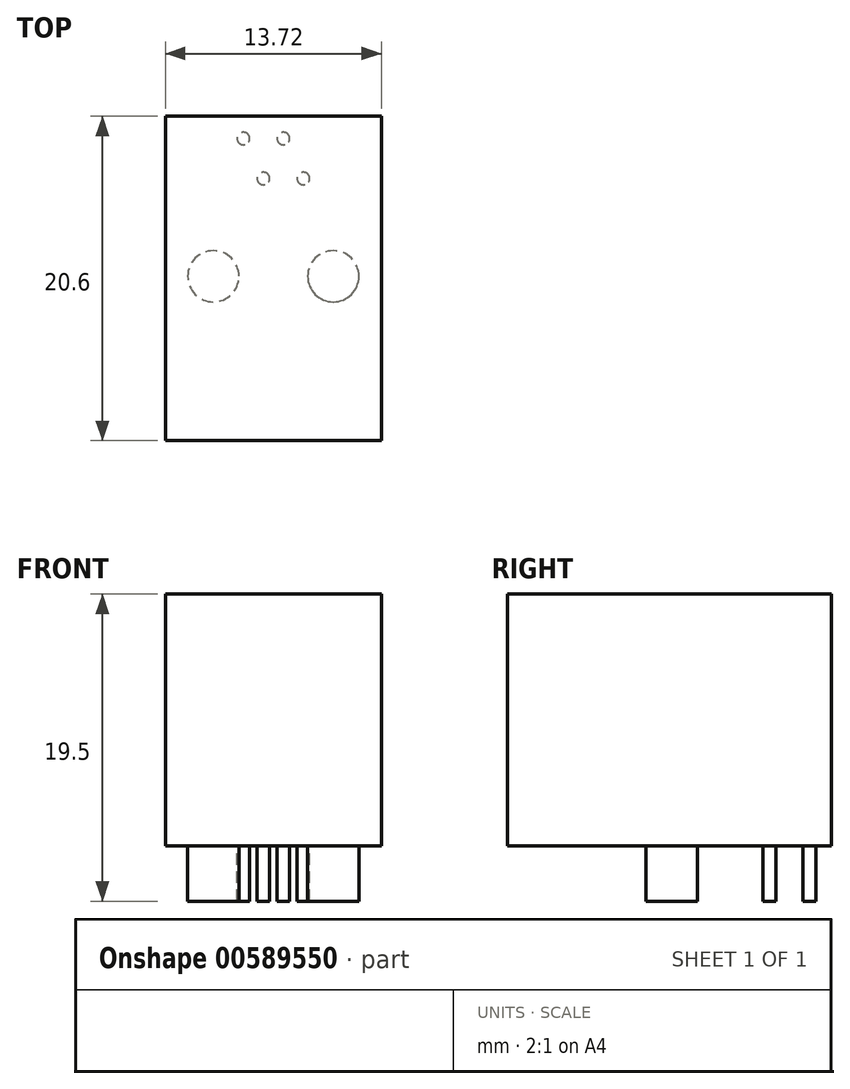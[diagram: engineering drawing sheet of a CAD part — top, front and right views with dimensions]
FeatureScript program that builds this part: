
annotation { "Feature Type Name" : "Feature", "Feature Type Description" : "" }
export const myFeature = defineFeature(function(context is Context, id is Id, definition is map)
    precondition{}
    {
        {
            var Q0;
            Q0=qCreatedBy(makeId("Top.planeOp"),FACE);
            var sketch = newSketch(context, id + "F0", { "sketchPlane" : qUnion([Q0])});
            skLineSegment(sketch, "E0.bottom", {"start": v(-6.86, 10.3) * mm, "end": v(6.86, 10.3) * mm});
            skLineSegment(sketch, "E0.top", {"start": v(-6.86, -10.3) * mm, "end": v(6.86, -10.3) * mm});
            skLineSegment(sketch, "E0.left", {"start": v(-6.86, 10.3) * mm, "end": v(-6.86, -10.3) * mm});
            skLineSegment(sketch, "E0.right", {"start": v(6.86, 10.3) * mm, "end": v(6.86, -10.3) * mm});
            skPoint(sketch, "E0.middle", {"position": v(0, 0) * mm});
            skSolve(sketch);
        }
        {
            var Q0;
            Q0 = qSketchRegion(id + "F0", true);
            extrude(context, id + "F1", {"entities" : qUnion([Q0]), "depth" : 16 * mm, "offsetDistance" : 25.4 * mm});
        }
        {
            var Q0;
            Q0=makeQuery(id+"F1.opExtrude","CAP_FACE",FACE,{"disambiguationData":[OSD([sQuery(id+"F0.wireOp",EDGE,"E0.bottom"),sQuery(id+"F0.wireOp",EDGE,"E0.top"),sQuery(id+"F0.wireOp",EDGE,"E0.left"),sQuery(id+"F0.wireOp",EDGE,"E0.right")])],"isStart":true});
            var sketch = newSketch(context, id + "F2", { "sketchPlane" : qUnion([Q0])});
            skCircle(sketch, "E1", {"center": v(-3.81, -0.14) * mm, "radius": 1.63 * mm});
            skCircle(sketch, "E2.MirrorC", {"center": v(3.81, -0.14) * mm, "radius": 1.63 * mm});
            skSolve(sketch);
        }
        {
            var Q0;
            Q0 = qSketchRegion(id + "F2", true);
            extrude(context, id + "F3", {"entities" : qUnion([Q0]), "operationType" : NewBodyOperationType.ADD, "depth" : 3.5 * mm, "offsetDistance" : 25 * mm});
        }
        {
            var Q0;
            Q0=makeQuery(id+"F1.opExtrude","CAP_FACE",FACE,{"disambiguationData":[OSD([sQuery(id+"F0.wireOp",EDGE,"E0.bottom"),sQuery(id+"F0.wireOp",EDGE,"E0.top"),sQuery(id+"F0.wireOp",EDGE,"E0.left"),sQuery(id+"F0.wireOp",EDGE,"E0.right")])],"isStart":true});
            var sketch = newSketch(context, id + "F4", { "sketchPlane" : qUnion([Q0])});
            skCircle(sketch, "E3", {"center": v(-0.63, -6.35) * mm, "radius": 0.4 * mm});
            skCircle(sketch, "E4", {"center": v(1.9, -6.35) * mm, "radius": 0.4 * mm});
            skCircle(sketch, "E5", {"center": v(-1.9, -8.89) * mm, "radius": 0.4 * mm});
            skCircle(sketch, "E6", {"center": v(0.64, -8.89) * mm, "radius": 0.4 * mm});
            skLineSegment(sketch, "E7", {"start": v(-0.63, -6.35) * mm, "end": v(-0.63, -8.89) * mm, "construction": true});
            skLineSegment(sketch, "E8", {"start": v(-0.63, -8.89) * mm, "end": v(-1.9, -8.89) * mm, "construction": true});
            skLineSegment(sketch, "E9", {"start": v(-0.63, -8.89) * mm, "end": v(0.64, -8.89) * mm, "construction": true});
            skLineSegment(sketch, "E10", {"start": v(0.64, -8.89) * mm, "end": v(0.64, -6.35) * mm, "construction": true});
            skLineSegment(sketch, "E11", {"start": v(1.9, -6.35) * mm, "end": v(0.64, -6.35) * mm, "construction": true});
            skLineSegment(sketch, "E12", {"start": v(-0.63, -6.35) * mm, "end": v(0.64, -8.89) * mm, "construction": true});
            skPoint(sketch, "E13", {"position": v(0, -7.62) * mm});
            skSolve(sketch);
        }
        {
            var Q0;
            Q0 = qSketchRegion(id + "F4", true);
            extrude(context, id + "F5", {"entities" : qUnion([Q0]), "operationType" : NewBodyOperationType.ADD, "depth" : 3.5 * mm, "offsetDistance" : 25 * mm});
        }
    });
